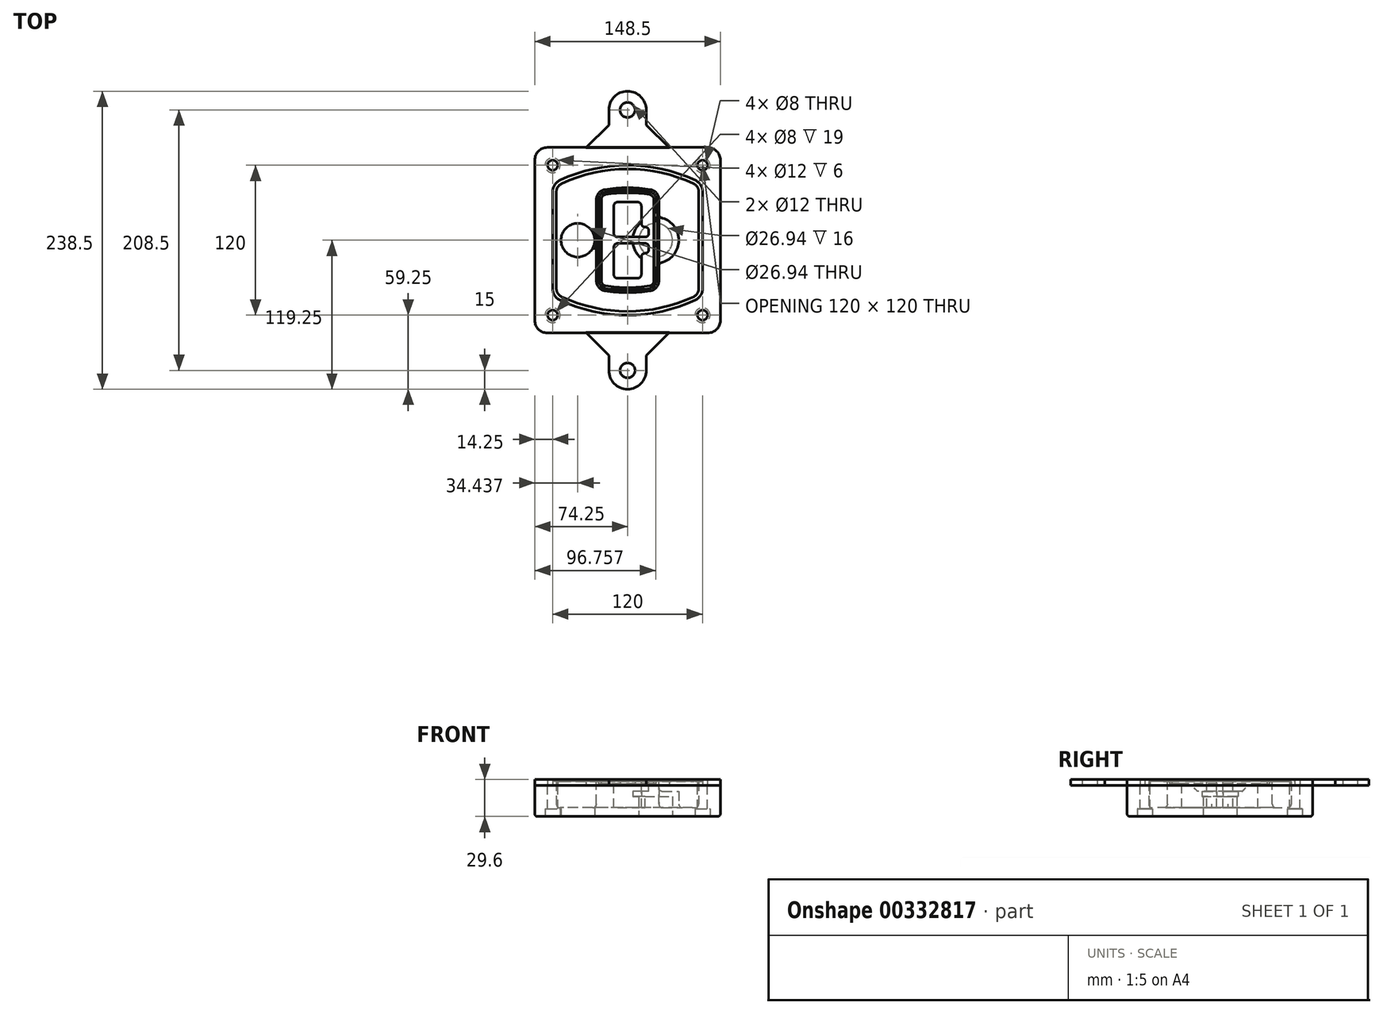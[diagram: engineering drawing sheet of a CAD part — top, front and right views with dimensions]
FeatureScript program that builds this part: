
annotation { "Feature Type Name" : "Feature", "Feature Type Description" : "" }
export const myFeature = defineFeature(function(context is Context, id is Id, definition is map)
    precondition{}
    {
        {
            var Q0;
            Q0=qCreatedBy(makeId("Top.planeOp"),FACE);
            var sketch = newSketch(context, id + "F0", { "sketchPlane" : qUnion([Q0])});
            skPoint(sketch, "E0.rect.middle", {"position": v(0, 0) * mm});
            skLineSegment(sketch, "E1.bottom", {"start": v(-64.25, -74.25) * mm, "end": v(64.25, -74.25) * mm});
            skLineSegment(sketch, "E1.top", {"start": v(-64.25, 74.25) * mm, "end": v(64.25, 74.25) * mm});
            skLineSegment(sketch, "E1.left", {"start": v(-74.25, -64.25) * mm, "end": v(-74.25, 64.25) * mm});
            skLineSegment(sketch, "E1.right", {"start": v(74.25, -64.25) * mm, "end": v(74.25, 64.25) * mm});
            skLineSegment(sketch, "E2", {"start": v(-74.25, 74.25) * mm, "end": v(74.25, -74.25) * mm, "construction": true});
            skLineSegment(sketch, "E3", {"start": v(74.25, 74.25) * mm, "end": v(-74.25, -74.25) * mm, "construction": true});
            skCircle(sketch, "E4", {"center": v(-60, 60) * mm, "radius": 4 * mm});
            skCircle(sketch, "E5", {"center": v(60, 60) * mm, "radius": 4 * mm});
            skCircle(sketch, "E6", {"center": v(60, -60) * mm, "radius": 4 * mm});
            skCircle(sketch, "E7", {"center": v(-60, -60) * mm, "radius": 4 * mm});
            skLineSegment(sketch, "E8", {"start": v(-60, 60) * mm, "end": v(60, 60) * mm, "construction": true});
            skLineSegment(sketch, "E9", {"start": v(60, 60) * mm, "end": v(60, -60) * mm, "construction": true});
            skLineSegment(sketch, "E10", {"start": v(60, -60) * mm, "end": v(-60, -60) * mm, "construction": true});
            skLineSegment(sketch, "E11", {"start": v(-60, -60) * mm, "end": v(-60, 60) * mm, "construction": true});
            skLineSegment(sketch, "E12", {"start": v(-60, 38.83) * mm, "end": v(-60, -38.83) * mm});
            skLineSegment(sketch, "E13", {"start": v(60, 38.83) * mm, "end": v(60, -38.83) * mm});
            skArc(sketch, "E14", {"start": v(54.26, 47.88) * mm, "mid": v(0, 60) * mm, "end": v(-54.26, 47.88) * mm});
            skArc(sketch, "E15", {"start": v(-54.26, -47.88) * mm, "mid": v(0, -60) * mm, "end": v(54.26, -47.88) * mm});
            skLineSegment(sketch, "E16", {"start": v(-60, 0) * mm, "end": v(60, 0) * mm, "construction": true});
            skPoint(sketch, "E17.visualSharp", {"position": v(-60, -45) * mm});
            skArc(sketch, "E17.filletArc", {"start": v(-60, -38.83) * mm, "mid": v(-58.44, -44.2) * mm, "end": v(-54.26, -47.88) * mm});
            skPoint(sketch, "E18.visualSharp", {"position": v(-60, 45) * mm});
            skArc(sketch, "E18.filletArc", {"start": v(-54.26, 47.88) * mm, "mid": v(-58.44, 44.2) * mm, "end": v(-60, 38.83) * mm});
            skPoint(sketch, "E19.visualSharp", {"position": v(60, 45) * mm});
            skArc(sketch, "E19.filletArc", {"start": v(60, 38.83) * mm, "mid": v(58.44, 44.2) * mm, "end": v(54.26, 47.88) * mm});
            skPoint(sketch, "E20.visualSharp", {"position": v(60, -45) * mm});
            skArc(sketch, "E20.filletArc", {"start": v(54.26, -47.88) * mm, "mid": v(58.44, -44.2) * mm, "end": v(60, -38.83) * mm});
            skPoint(sketch, "E21.visualSharp", {"position": v(-74.25, 74.25) * mm});
            skArc(sketch, "E21.filletArc", {"start": v(-64.25, 74.25) * mm, "mid": v(-71.32, 71.32) * mm, "end": v(-74.25, 64.25) * mm});
            skPoint(sketch, "E22.visualSharp", {"position": v(74.25, 74.25) * mm});
            skArc(sketch, "E22.filletArc", {"start": v(74.25, 64.25) * mm, "mid": v(71.32, 71.32) * mm, "end": v(64.25, 74.25) * mm});
            skPoint(sketch, "E23.visualSharp", {"position": v(74.25, -74.25) * mm});
            skArc(sketch, "E23.filletArc", {"start": v(64.25, -74.25) * mm, "mid": v(71.32, -71.32) * mm, "end": v(74.25, -64.25) * mm});
            skPoint(sketch, "E24.visualSharp", {"position": v(-74.25, -74.25) * mm});
            skArc(sketch, "E24.filletArc", {"start": v(-74.25, -64.25) * mm, "mid": v(-71.32, -71.32) * mm, "end": v(-64.25, -74.25) * mm});
            skArc(sketch, "E25.0", {"start": v(57, 38.83) * mm, "mid": v(55.9, 42.58) * mm, "end": v(52.98, 45.17) * mm});
            skLineSegment(sketch, "E25.1", {"start": v(57, 38.83) * mm, "end": v(57, -38.83) * mm});
            skArc(sketch, "E25.2", {"start": v(52.98, -45.17) * mm, "mid": v(55.9, -42.58) * mm, "end": v(57, -38.83) * mm});
            skArc(sketch, "E25.3", {"start": v(-52.98, -45.17) * mm, "mid": v(0, -57) * mm, "end": v(52.98, -45.17) * mm});
            skArc(sketch, "E25.4", {"start": v(-57, -38.83) * mm, "mid": v(-55.9, -42.58) * mm, "end": v(-52.98, -45.17) * mm});
            skArc(sketch, "E25.5", {"start": v(52.98, 45.17) * mm, "mid": v(0, 57) * mm, "end": v(-52.98, 45.17) * mm});
            skLineSegment(sketch, "E25.6", {"start": v(-57, 38.83) * mm, "end": v(-57, -38.83) * mm});
            skArc(sketch, "E25.7", {"start": v(-52.98, 45.17) * mm, "mid": v(-55.9, 42.58) * mm, "end": v(-57, 38.83) * mm});
            skArc(sketch, "E26.0", {"start": v(-55.96, 51.5) * mm, "mid": v(-61.82, 46.33) * mm, "end": v(-64, 38.83) * mm});
            skArc(sketch, "E26.1", {"start": v(55.96, 51.5) * mm, "mid": v(0, 64) * mm, "end": v(-55.96, 51.5) * mm});
            skArc(sketch, "E26.2", {"start": v(64, 38.83) * mm, "mid": v(61.82, 46.33) * mm, "end": v(55.96, 51.5) * mm});
            skLineSegment(sketch, "E26.3", {"start": v(64, 38.83) * mm, "end": v(64, -38.83) * mm});
            skArc(sketch, "E26.4", {"start": v(55.96, -51.5) * mm, "mid": v(61.82, -46.33) * mm, "end": v(64, -38.83) * mm});
            skLineSegment(sketch, "E26.5", {"start": v(-64, 38.83) * mm, "end": v(-64, -38.83) * mm});
            skArc(sketch, "E26.6", {"start": v(-55.96, -51.5) * mm, "mid": v(0, -64) * mm, "end": v(55.96, -51.5) * mm});
            skArc(sketch, "E26.7", {"start": v(-64, -38.83) * mm, "mid": v(-61.82, -46.33) * mm, "end": v(-55.96, -51.5) * mm});
            skSolve(sketch);
        }
        {
            var Q0;
            Q0=makeQuery(id+"F0.imprint","IMPRINT",FACE,{"disambiguationData":[TD([[makeQuery(id+"F0.imprint","IMPRINT",EDGE,{"derivedFrom":sQuery(id+"F0.wireOp",EDGE,"E1.bottom")}),1.0]])]});
            var Q1;
            Q1=makeQuery(id+"F0.imprint","IMPRINT",FACE,{"disambiguationData":[TD([[makeQuery(id+"F0.imprint","IMPRINT",EDGE,{"derivedFrom":sQuery(id+"F0.wireOp",EDGE,"E12")}),1.0]])]});
            var Q2;
            Q2=makeQuery(id+"F0.imprint","IMPRINT",FACE,{"disambiguationData":[TD([[makeQuery(id+"F0.imprint","IMPRINT",EDGE,{"derivedFrom":sQuery(id+"F0.wireOp",EDGE,"E25.0")}),1.0]])]});
            var Q3;
            Q3=makeQuery(id+"F0.imprint","IMPRINT",FACE,{"disambiguationData":[TD([[makeQuery(id+"F0.imprint","IMPRINT",EDGE,{"derivedFrom":sQuery(id+"F0.wireOp",EDGE,"E12")}),-1.0]])]});
            extrude(context, id + "F1", {"entities" : qUnion([Q0, Q1, Q2, Q3]), "oppositeDirection" : true, "depth" : 25 * mm});
        }
        {
            var Q0;
            Q0=makeQuery(id+"F0.imprint","IMPRINT",FACE,{"disambiguationData":[TD([[makeQuery(id+"F0.imprint","IMPRINT",EDGE,{"derivedFrom":sQuery(id+"F0.wireOp",EDGE,"E12")}),1.0]])]});
            extrude(context, id + "F2", {"entities" : qUnion([Q0]), "operationType" : NewBodyOperationType.ADD, "depth" : 3 * mm});
        }
        {
            var Q0;
            Q0=makeQuery(id+"F0.imprint","IMPRINT",FACE,{"disambiguationData":[TD([[makeQuery(id+"F0.imprint","IMPRINT",EDGE,{"derivedFrom":sQuery(id+"F0.wireOp",EDGE,"E25.0")}),1.0]])]});
            extrude(context, id + "F3", {"entities" : qUnion([Q0]), "operationType" : NewBodyOperationType.REMOVE, "oppositeDirection" : true, "depth" : 18 * mm});
        }
        {
            var Q0;
            Q0=makeQuery(id+"F2.opExtrude","CAP_FACE",FACE,{"disambiguationData":[OSD([sQuery(id+"F0.wireOp",EDGE,"E12"),sQuery(id+"F0.wireOp",EDGE,"E13"),sQuery(id+"F0.wireOp",EDGE,"E14"),sQuery(id+"F0.wireOp",EDGE,"E15"),sQuery(id+"F0.wireOp",EDGE,"E17.filletArc"),sQuery(id+"F0.wireOp",EDGE,"E18.filletArc"),sQuery(id+"F0.wireOp",EDGE,"E19.filletArc"),sQuery(id+"F0.wireOp",EDGE,"E20.filletArc"),sQuery(id+"F0.wireOp",EDGE,"E25.0"),sQuery(id+"F0.wireOp",EDGE,"E25.1"),sQuery(id+"F0.wireOp",EDGE,"E25.2"),sQuery(id+"F0.wireOp",EDGE,"E25.3"),sQuery(id+"F0.wireOp",EDGE,"E25.4"),sQuery(id+"F0.wireOp",EDGE,"E25.5"),sQuery(id+"F0.wireOp",EDGE,"E25.6"),sQuery(id+"F0.wireOp",EDGE,"E25.7")])],"isStart":false});
            var sketch = newSketch(context, id + "F4", { "sketchPlane" : qUnion([Q0])});
            skArc(sketch, "E27.0", {"start": v(-18.34, -40.45) * mm, "mid": v(0, -42) * mm, "end": v(18.34, -40.45) * mm});
            skArc(sketch, "E28.0", {"start": v(18.34, 40.45) * mm, "mid": v(0, 42) * mm, "end": v(-18.34, 40.45) * mm});
            skLineSegment(sketch, "E29", {"start": v(-25, 32.57) * mm, "end": v(-25, -32.57) * mm});
            skLineSegment(sketch, "E30", {"start": v(25, 32.57) * mm, "end": v(25, -32.57) * mm});
            skLineSegment(sketch, "E31", {"start": v(-25, 39.1) * mm, "end": v(25, 39.1) * mm, "construction": true});
            skLineSegment(sketch, "E32", {"start": v(-25, -39.1) * mm, "end": v(25, -39.1) * mm, "construction": true});
            skPoint(sketch, "E33.visualSharp", {"position": v(-25, 39.1) * mm});
            skArc(sketch, "E33.filletArc", {"start": v(-18.34, 40.45) * mm, "mid": v(-23.11, 37.73) * mm, "end": v(-25, 32.57) * mm});
            skPoint(sketch, "E34.visualSharp", {"position": v(25, 39.1) * mm});
            skArc(sketch, "E34.filletArc", {"start": v(25, 32.57) * mm, "mid": v(23.11, 37.73) * mm, "end": v(18.34, 40.45) * mm});
            skPoint(sketch, "E35.visualSharp", {"position": v(25, -39.1) * mm});
            skArc(sketch, "E35.filletArc", {"start": v(18.34, -40.45) * mm, "mid": v(23.11, -37.73) * mm, "end": v(25, -32.57) * mm});
            skPoint(sketch, "E36.visualSharp", {"position": v(-25, -39.1) * mm});
            skArc(sketch, "E36.filletArc", {"start": v(-25, -32.57) * mm, "mid": v(-23.11, -37.73) * mm, "end": v(-18.34, -40.45) * mm});
            skArc(sketch, "E37.0", {"start": v(52.98, 45.17) * mm, "mid": v(0, 57) * mm, "end": v(-52.98, 45.17) * mm});
            skArc(sketch, "E37.1", {"start": v(-52.98, 45.17) * mm, "mid": v(-55.9, 42.58) * mm, "end": v(-57, 38.83) * mm});
            skLineSegment(sketch, "E37.2", {"start": v(-57, 38.83) * mm, "end": v(-57, -38.83) * mm});
            skArc(sketch, "E37.3", {"start": v(-57, -38.83) * mm, "mid": v(-55.9, -42.58) * mm, "end": v(-52.98, -45.17) * mm});
            skArc(sketch, "E37.4", {"start": v(-52.98, -45.17) * mm, "mid": v(0, -57) * mm, "end": v(52.98, -45.17) * mm});
            skArc(sketch, "E37.5", {"start": v(52.98, -45.17) * mm, "mid": v(55.9, -42.58) * mm, "end": v(57, -38.83) * mm});
            skLineSegment(sketch, "E37.6", {"start": v(57, 38.83) * mm, "end": v(57, -38.83) * mm});
            skArc(sketch, "E37.7", {"start": v(57, 38.83) * mm, "mid": v(55.9, 42.58) * mm, "end": v(52.98, 45.17) * mm});
            skLineSegment(sketch, "E38.0", {"start": v(23, 32.57) * mm, "end": v(23, -32.57) * mm});
            skArc(sketch, "E38.1", {"start": v(18, -38.48) * mm, "mid": v(21.58, -36.44) * mm, "end": v(23, -32.57) * mm});
            skArc(sketch, "E38.2", {"start": v(-18, -38.48) * mm, "mid": v(0, -40) * mm, "end": v(18, -38.48) * mm});
            skArc(sketch, "E38.3", {"start": v(-23, -32.57) * mm, "mid": v(-21.58, -36.44) * mm, "end": v(-18, -38.48) * mm});
            skLineSegment(sketch, "E38.4", {"start": v(-23, 32.57) * mm, "end": v(-23, -32.57) * mm});
            skArc(sketch, "E38.5", {"start": v(23, 32.57) * mm, "mid": v(21.58, 36.44) * mm, "end": v(18, 38.48) * mm});
            skArc(sketch, "E38.6", {"start": v(-18, 38.48) * mm, "mid": v(-21.58, 36.44) * mm, "end": v(-23, 32.57) * mm});
            skArc(sketch, "E38.7", {"start": v(18, 38.48) * mm, "mid": v(0, 40) * mm, "end": v(-18, 38.48) * mm});
            skArc(sketch, "E39.0", {"start": v(21, 32.57) * mm, "mid": v(20.06, 35.15) * mm, "end": v(17.67, 36.5) * mm});
            skLineSegment(sketch, "E39.1", {"start": v(21, 32.57) * mm, "end": v(21, -32.57) * mm});
            skArc(sketch, "E39.2", {"start": v(17.67, -36.5) * mm, "mid": v(20.06, -35.15) * mm, "end": v(21, -32.57) * mm});
            skArc(sketch, "E39.3", {"start": v(-17.67, -36.5) * mm, "mid": v(0, -38) * mm, "end": v(17.67, -36.5) * mm});
            skArc(sketch, "E39.4", {"start": v(-21, -32.57) * mm, "mid": v(-20.06, -35.15) * mm, "end": v(-17.67, -36.5) * mm});
            skArc(sketch, "E39.5", {"start": v(17.67, 36.5) * mm, "mid": v(0, 38) * mm, "end": v(-17.67, 36.5) * mm});
            skLineSegment(sketch, "E39.6", {"start": v(-21, 32.57) * mm, "end": v(-21, -32.57) * mm});
            skArc(sketch, "E39.7", {"start": v(-17.67, 36.5) * mm, "mid": v(-20.06, 35.15) * mm, "end": v(-21, 32.57) * mm});
            skLineSegment(sketch, "E40", {"start": v(-25, 0) * mm, "end": v(25, 0) * mm, "construction": true});
            skLineSegment(sketch, "E41", {"start": v(-11, 5.5) * mm, "end": v(-11, 27.5) * mm});
            skLineSegment(sketch, "E42", {"start": v(-8, 30.5) * mm, "end": v(8, 30.5) * mm});
            skLineSegment(sketch, "E43", {"start": v(11, 27.5) * mm, "end": v(11, 13.5) * mm});
            skLineSegment(sketch, "E44", {"start": v(14, 10.5) * mm, "end": v(14, 10.5) * mm});
            skLineSegment(sketch, "E45", {"start": v(17, 7.5) * mm, "end": v(17, 5.5) * mm});
            skLineSegment(sketch, "E46", {"start": v(14, 2.5) * mm, "end": v(-8, 2.5) * mm});
            skPoint(sketch, "E47.visualSharp", {"position": v(-11, 30.5) * mm});
            skArc(sketch, "E47.filletArc", {"start": v(-8, 30.5) * mm, "mid": v(-10.12, 29.62) * mm, "end": v(-11, 27.5) * mm});
            skPoint(sketch, "E48.visualSharp", {"position": v(11, 30.5) * mm});
            skArc(sketch, "E48.filletArc", {"start": v(11, 27.5) * mm, "mid": v(10.12, 29.62) * mm, "end": v(8, 30.5) * mm});
            skPoint(sketch, "E49.visualSharp", {"position": v(11, 10.5) * mm});
            skArc(sketch, "E49.filletArc", {"start": v(11, 13.5) * mm, "mid": v(11.88, 11.38) * mm, "end": v(14, 10.5) * mm});
            skPoint(sketch, "E50.visualSharp", {"position": v(17, 10.5) * mm});
            skArc(sketch, "E50.filletArc", {"start": v(17, 7.5) * mm, "mid": v(16.12, 9.62) * mm, "end": v(14, 10.5) * mm});
            skPoint(sketch, "E51.visualSharp", {"position": v(17, 2.5) * mm});
            skArc(sketch, "E51.filletArc", {"start": v(14, 2.5) * mm, "mid": v(16.12, 3.38) * mm, "end": v(17, 5.5) * mm});
            skPoint(sketch, "E52.visualSharp", {"position": v(-11, 2.5) * mm});
            skArc(sketch, "E52.filletArc", {"start": v(-11, 5.5) * mm, "mid": v(-10.12, 3.38) * mm, "end": v(-8, 2.5) * mm});
            skLineSegment(sketch, "E53.0.MirrorCS", {"start": v(14, -2.5) * mm, "end": v(-8, -2.5) * mm});
            skArc(sketch, "E54.0.MirrorCS", {"start": v(-11, -5.5) * mm, "mid": v(-10.12, -3.38) * mm, "end": v(-8, -2.5) * mm});
            skLineSegment(sketch, "E55.0.MirrorCS", {"start": v(-11, -5.5) * mm, "end": v(-11, -27.5) * mm});
            skArc(sketch, "E56.0.MirrorCS", {"start": v(-8, -30.5) * mm, "mid": v(-10.12, -29.62) * mm, "end": v(-11, -27.5) * mm});
            skLineSegment(sketch, "E57.0.MirrorCS", {"start": v(-8, -30.5) * mm, "end": v(8, -30.5) * mm});
            skArc(sketch, "E58.0.MirrorCS", {"start": v(11, -27.5) * mm, "mid": v(10.12, -29.62) * mm, "end": v(8, -30.5) * mm});
            skLineSegment(sketch, "E59.0.MirrorCS", {"start": v(11, -27.5) * mm, "end": v(11, -13.5) * mm});
            skArc(sketch, "E60.0.MirrorCS", {"start": v(11, -13.5) * mm, "mid": v(11.88, -11.38) * mm, "end": v(14, -10.5) * mm});
            skArc(sketch, "E61.0.MirrorCS", {"start": v(17, -7.5) * mm, "mid": v(16.12, -9.62) * mm, "end": v(14, -10.5) * mm});
            skLineSegment(sketch, "E62.0.MirrorCS", {"start": v(17, -7.5) * mm, "end": v(17, -5.5) * mm});
            skArc(sketch, "E63.0.MirrorCS", {"start": v(14, -2.5) * mm, "mid": v(16.12, -3.38) * mm, "end": v(17, -5.5) * mm});
            skSolve(sketch);
        }
        {
            var Q0;
            Q0=makeQuery(id+"F4.imprint","IMPRINT",FACE,{"disambiguationData":[TD([[makeQuery(id+"F4.imprint","IMPRINT",EDGE,{"derivedFrom":sQuery(id+"F4.wireOp",EDGE,"E27.0")}),1.0]])]});
            var Q1;
            Q1=makeQuery(id+"F4.imprint","IMPRINT",FACE,{"disambiguationData":[TD([[makeQuery(id+"F4.imprint","IMPRINT",EDGE,{"derivedFrom":sQuery(id+"F4.wireOp",EDGE,"E38.0")}),-1.0]])]});
            var Q2;
            Q2=makeQuery(id+"F4.imprint","IMPRINT",FACE,{"disambiguationData":[TD([[makeQuery(id+"F4.imprint","IMPRINT",EDGE,{"derivedFrom":sQuery(id+"F4.wireOp",EDGE,"E39.0")}),1.0]])]});
            extrude(context, id + "F5", {"entities" : qUnion([Q0, Q1, Q2]), "operationType" : NewBodyOperationType.ADD, "endBound" : BoundingType.UP_TO_NEXT, "oppositeDirection" : true, "depth" : 25 * mm});
        }
        {
            var Q0;
            Q0=makeQuery(id+"F4.imprint","IMPRINT",FACE,{"disambiguationData":[TD([[makeQuery(id+"F4.imprint","IMPRINT",EDGE,{"derivedFrom":sQuery(id+"F4.wireOp",EDGE,"E38.0")}),-1.0]])]});
            extrude(context, id + "F6", {"entities" : qUnion([Q0]), "operationType" : NewBodyOperationType.REMOVE, "oppositeDirection" : true, "depth" : 2 * mm});
        }
        {
            var Q0;
            Q0=makeQuery(id+"F1.opExtrude","CAP_FACE",FACE,{"disambiguationData":[OSD([sQuery(id+"F0.wireOp",EDGE,"E1.bottom"),sQuery(id+"F0.wireOp",EDGE,"E1.top"),sQuery(id+"F0.wireOp",EDGE,"E1.left"),sQuery(id+"F0.wireOp",EDGE,"E1.right"),sQuery(id+"F0.wireOp",EDGE,"E4"),sQuery(id+"F0.wireOp",EDGE,"E5"),sQuery(id+"F0.wireOp",EDGE,"E6"),sQuery(id+"F0.wireOp",EDGE,"E7"),sQuery(id+"F0.wireOp",EDGE,"E21.filletArc"),sQuery(id+"F0.wireOp",EDGE,"E22.filletArc"),sQuery(id+"F0.wireOp",EDGE,"E23.filletArc"),sQuery(id+"F0.wireOp",EDGE,"E24.filletArc")])],"isStart":false});
            var sketch = newSketch(context, id + "F7", { "sketchPlane" : qUnion([Q0])});
            skCircle(sketch, "E64", {"center": v(22.5, 0) * mm, "radius": 13.47 * mm});
            skCircle(sketch, "E65", {"center": v(-39.81, 0) * mm, "radius": 13.47 * mm});
            skLineSegment(sketch, "E66", {"start": v(74.25, 0) * mm, "end": v(-74.25, 0) * mm});
            skCircle(sketch, "E67", {"center": v(22.5, 0) * mm, "radius": 18.47 * mm});
            skCircle(sketch, "E68", {"center": v(60, -60) * mm, "radius": 6 * mm});
            skCircle(sketch, "E69", {"center": v(-60, -60) * mm, "radius": 6 * mm});
            skCircle(sketch, "E70", {"center": v(-60, 60) * mm, "radius": 6 * mm});
            skCircle(sketch, "E71", {"center": v(60, 60) * mm, "radius": 6 * mm});
            skSolve(sketch);
        }
        {
            var Q0;
            {var subQ1=sQuery(id+"F7.wireOp",EDGE,"E66");var subQ4=sQuery(id+"F7.wireOp",EDGE,"E64");var subQ6=makeQuery(id+"F7.imprint","INTERSECT",VERTEX,{"disambiguationData":[OD(0.0)],"derivedFrom":[subQ4,subQ1]});Q0=makeQuery(id+"F7.imprint","IMPRINT",FACE,{"disambiguationData":[TD([[makeQuery(id+"F7.imprint","IMPRINT",EDGE,{"disambiguationData":[TD([[subQ6,-1.0]])],"derivedFrom":subQ4}),-1.0]])]});}
            var Q1;
            {var subQ0=sQuery(id+"F7.wireOp",EDGE,"E66");var subQ1=sQuery(id+"F7.wireOp",EDGE,"E64");var subQ3=makeQuery(id+"F7.imprint","INTERSECT",VERTEX,{"disambiguationData":[OD(0.0)],"derivedFrom":[subQ1,subQ0]});Q1=makeQuery(id+"F7.imprint","IMPRINT",FACE,{"disambiguationData":[TD([[makeQuery(id+"F7.imprint","IMPRINT",EDGE,{"disambiguationData":[TD([[subQ3,-1.0]])],"derivedFrom":subQ1}),1.0]])]});}
            var Q2;
            {var subQ0=sQuery(id+"F7.wireOp",EDGE,"E66");var subQ1=sQuery(id+"F7.wireOp",EDGE,"E64");var subQ3=makeQuery(id+"F7.imprint","INTERSECT",VERTEX,{"disambiguationData":[OD(0.0)],"derivedFrom":[subQ1,subQ0]});Q2=makeQuery(id+"F7.imprint","IMPRINT",FACE,{"disambiguationData":[TD([[makeQuery(id+"F7.imprint","IMPRINT",EDGE,{"disambiguationData":[TD([[subQ3,1.0]])],"derivedFrom":subQ1}),1.0]])]});}
            var Q3;
            {var subQ1=sQuery(id+"F7.wireOp",EDGE,"E66");var subQ4=sQuery(id+"F7.wireOp",EDGE,"E64");var subQ6=makeQuery(id+"F7.imprint","INTERSECT",VERTEX,{"disambiguationData":[OD(0.0)],"derivedFrom":[subQ4,subQ1]});Q3=makeQuery(id+"F7.imprint","IMPRINT",FACE,{"disambiguationData":[TD([[makeQuery(id+"F7.imprint","IMPRINT",EDGE,{"disambiguationData":[TD([[subQ6,1.0]])],"derivedFrom":subQ4}),-1.0]])]});}
            extrude(context, id + "F8", {"entities" : qUnion([Q0, Q1, Q2, Q3]), "operationType" : NewBodyOperationType.ADD, "oppositeDirection" : true, "depth" : 20 * mm});
        }
        {
            var Q0;
            {var subQ0=sQuery(id+"F7.wireOp",EDGE,"E66");var subQ1=sQuery(id+"F7.wireOp",EDGE,"E64");var subQ3=makeQuery(id+"F7.imprint","INTERSECT",VERTEX,{"disambiguationData":[OD(0.0)],"derivedFrom":[subQ1,subQ0]});Q0=makeQuery(id+"F7.imprint","IMPRINT",FACE,{"disambiguationData":[TD([[makeQuery(id+"F7.imprint","IMPRINT",EDGE,{"disambiguationData":[TD([[subQ3,-1.0]])],"derivedFrom":subQ1}),1.0]])]});}
            var Q1;
            {var subQ0=sQuery(id+"F7.wireOp",EDGE,"E66");var subQ1=sQuery(id+"F7.wireOp",EDGE,"E64");var subQ3=makeQuery(id+"F7.imprint","INTERSECT",VERTEX,{"disambiguationData":[OD(0.0)],"derivedFrom":[subQ1,subQ0]});Q1=makeQuery(id+"F7.imprint","IMPRINT",FACE,{"disambiguationData":[TD([[makeQuery(id+"F7.imprint","IMPRINT",EDGE,{"disambiguationData":[TD([[subQ3,1.0]])],"derivedFrom":subQ1}),1.0]])]});}
            extrude(context, id + "F9", {"entities" : qUnion([Q0, Q1]), "operationType" : NewBodyOperationType.REMOVE, "oppositeDirection" : true, "depth" : 16 * mm});
        }
        {
            var Q0;
            {var subQ0=sQuery(id+"F7.wireOp",EDGE,"E66");var subQ1=sQuery(id+"F7.wireOp",EDGE,"E65");var subQ3=makeQuery(id+"F7.imprint","INTERSECT",VERTEX,{"disambiguationData":[OD(0.0)],"derivedFrom":[subQ1,subQ0]});Q0=makeQuery(id+"F7.imprint","IMPRINT",FACE,{"disambiguationData":[TD([[makeQuery(id+"F7.imprint","IMPRINT",EDGE,{"disambiguationData":[TD([[subQ3,-1.0]])],"derivedFrom":subQ1}),1.0]])]});}
            var Q1;
            {var subQ0=sQuery(id+"F7.wireOp",EDGE,"E66");var subQ1=sQuery(id+"F7.wireOp",EDGE,"E65");var subQ3=makeQuery(id+"F7.imprint","INTERSECT",VERTEX,{"disambiguationData":[OD(0.0)],"derivedFrom":[subQ1,subQ0]});Q1=makeQuery(id+"F7.imprint","IMPRINT",FACE,{"disambiguationData":[TD([[makeQuery(id+"F7.imprint","IMPRINT",EDGE,{"disambiguationData":[TD([[subQ3,1.0]])],"derivedFrom":subQ1}),1.0]])]});}
            extrude(context, id + "F10", {"entities" : qUnion([Q0, Q1]), "operationType" : NewBodyOperationType.REMOVE, "oppositeDirection" : true, "depth" : 25 * mm});
        }
        {
            var Q0;
            Q0=makeQuery(id+"F7.imprint","IMPRINT",FACE,{"disambiguationData":[TD([[makeQuery(id+"F7.imprint","IMPRINT",EDGE,{"derivedFrom":sQuery(id+"F7.wireOp",EDGE,"E68")}),1.0]])]});
            var Q1;
            Q1=makeQuery(id+"F7.imprint","IMPRINT",FACE,{"disambiguationData":[TD([[makeQuery(id+"F7.imprint","IMPRINT",EDGE,{"derivedFrom":makeQuery(id+"F1.opExtrude","CAP_EDGE",EDGE,{"disambiguationData":[OSD([sQuery(id+"F0.wireOp",EDGE,"E5")])],"isStart":false})}),-1.0]])]});
            var Q2;
            Q2=makeQuery(id+"F7.imprint","IMPRINT",FACE,{"disambiguationData":[TD([[makeQuery(id+"F7.imprint","IMPRINT",EDGE,{"derivedFrom":sQuery(id+"F7.wireOp",EDGE,"E69")}),1.0]])]});
            var Q3;
            Q3=makeQuery(id+"F7.imprint","IMPRINT",FACE,{"disambiguationData":[TD([[makeQuery(id+"F7.imprint","IMPRINT",EDGE,{"derivedFrom":makeQuery(id+"F1.opExtrude","CAP_EDGE",EDGE,{"disambiguationData":[OSD([sQuery(id+"F0.wireOp",EDGE,"E4")])],"isStart":false})}),-1.0]])]});
            var Q4;
            Q4=makeQuery(id+"F7.imprint","IMPRINT",FACE,{"disambiguationData":[TD([[makeQuery(id+"F7.imprint","IMPRINT",EDGE,{"derivedFrom":sQuery(id+"F7.wireOp",EDGE,"E70")}),1.0]])]});
            var Q5;
            Q5=makeQuery(id+"F7.imprint","IMPRINT",FACE,{"disambiguationData":[TD([[makeQuery(id+"F7.imprint","IMPRINT",EDGE,{"derivedFrom":makeQuery(id+"F1.opExtrude","CAP_EDGE",EDGE,{"disambiguationData":[OSD([sQuery(id+"F0.wireOp",EDGE,"E7")])],"isStart":false})}),-1.0]])]});
            var Q6;
            Q6=makeQuery(id+"F7.imprint","IMPRINT",FACE,{"disambiguationData":[TD([[makeQuery(id+"F7.imprint","IMPRINT",EDGE,{"derivedFrom":sQuery(id+"F7.wireOp",EDGE,"E71")}),1.0]])]});
            var Q7;
            Q7=makeQuery(id+"F7.imprint","IMPRINT",FACE,{"disambiguationData":[TD([[makeQuery(id+"F7.imprint","IMPRINT",EDGE,{"derivedFrom":makeQuery(id+"F1.opExtrude","CAP_EDGE",EDGE,{"disambiguationData":[OSD([sQuery(id+"F0.wireOp",EDGE,"E6")])],"isStart":false})}),-1.0]])]});
            extrude(context, id + "F11", {"entities" : qUnion([Q0, Q1, Q2, Q3, Q4, Q5, Q6, Q7]), "operationType" : NewBodyOperationType.REMOVE, "oppositeDirection" : true, "depth" : 6 * mm});
        }
        {
            var Q0;
            Q0=makeQuery(id+"F9.boolean.opBoolean","COPY",FACE,{"derivedFrom":makeQuery(id+"F9.opExtrude","CAP_FACE",FACE,{"disambiguationData":[OSD([sQuery(id+"F7.wireOp",EDGE,"E64")])],"isStart":false})});
            var sketch = newSketch(context, id + "F12", { "sketchPlane" : qUnion([Q0])});
            skArc(sketch, "E72.0", {"start": v(11, 14.45) * mm, "mid": v(6.45, 9.13) * mm, "end": v(4.2, 2.5) * mm});
            skArc(sketch, "E72.1", {"start": v(4.2, -2.5) * mm, "mid": v(6.45, -9.13) * mm, "end": v(11, -14.45) * mm});
            skLineSegment(sketch, "E73", {"start": v(4.2, -2.5) * mm, "end": v(14, -2.5) * mm});
            skLineSegment(sketch, "E74.0", {"start": v(14, 2.5) * mm, "end": v(4.2, 2.5) * mm});
            skArc(sketch, "E74.1", {"start": v(14, 2.5) * mm, "mid": v(16.12, 3.38) * mm, "end": v(17, 5.5) * mm});
            skLineSegment(sketch, "E74.2", {"start": v(17, 7.5) * mm, "end": v(17, 5.5) * mm});
            skArc(sketch, "E74.3", {"start": v(17, 7.5) * mm, "mid": v(16.12, 9.62) * mm, "end": v(14, 10.5) * mm});
            skArc(sketch, "E74.4", {"start": v(11, 13.5) * mm, "mid": v(11.88, 11.38) * mm, "end": v(14, 10.5) * mm});
            skLineSegment(sketch, "E74.5", {"start": v(11, 14.45) * mm, "end": v(11, 13.5) * mm});
            skLineSegment(sketch, "E74.7", {"start": v(14, -2.5) * mm, "end": v(4.2, -2.5) * mm});
            skArc(sketch, "E74.8", {"start": v(14, -2.5) * mm, "mid": v(16.12, -3.38) * mm, "end": v(17, -5.5) * mm});
            skLineSegment(sketch, "E74.9", {"start": v(17, -7.5) * mm, "end": v(17, -5.5) * mm});
            skArc(sketch, "E74.10", {"start": v(17, -7.5) * mm, "mid": v(16.12, -9.62) * mm, "end": v(14, -10.5) * mm});
            skArc(sketch, "E74.11", {"start": v(11, -13.5) * mm, "mid": v(11.88, -11.38) * mm, "end": v(14, -10.5) * mm});
            skLineSegment(sketch, "E74.12", {"start": v(11, -14.45) * mm, "end": v(11, -13.5) * mm});
            skPoint(sketch, "E75.orphan", {"position": v(11, -27.5) * mm});
            skPoint(sketch, "E76.orphan", {"position": v(-8, -2.5) * mm});
            skPoint(sketch, "E77.orphan", {"position": v(-8, 2.5) * mm});
            skPoint(sketch, "E78.orphan", {"position": v(11, 27.5) * mm});
            skSolve(sketch);
        }
        {
            var Q0;
            {var subQ7=sQuery(id+"F12.wireOp",EDGE,"E72.0");var subQ14=sQuery(id+"F12.wireOp",EDGE,"E72.1");var subQ16=sQuery(id+"F12.wireOp",EDGE,"E74.1");var subQ18=sQuery(id+"F12.wireOp",EDGE,"E74.8");Q0=qUnion([makeQuery(id+"F12.imprint","IMPRINT",FACE,{"disambiguationData":[TD([[makeQuery(id+"F12.imprint","IMPRINT",EDGE,{"derivedFrom":subQ7}),1.0]])]}),makeQuery(id+"F12.imprint","IMPRINT",FACE,{"disambiguationData":[TD([[makeQuery(id+"F12.imprint","IMPRINT",EDGE,{"derivedFrom":subQ14}),1.0]])]}),makeQuery(id+"F12.imprint","IMPRINT",FACE,{"disambiguationData":[TD([[makeQuery(id+"F12.imprint","IMPRINT",EDGE,{"derivedFrom":subQ16}),1.0]])]}),makeQuery(id+"F12.imprint","IMPRINT",FACE,{"disambiguationData":[TD([[makeQuery(id+"F12.imprint","IMPRINT",EDGE,{"derivedFrom":subQ18}),-1.0]])]})]);}
            var Q1;
            Q1=makeQuery(id+"F5.boolean.opBoolean","SPLIT",FACE,{"disambiguationData":[TD([makeQuery(id+"F5.opExtrude","SWEPT_FACE",FACE,{"disambiguationData":[OSD([sQuery(id+"F4.wireOp",EDGE,"E41")])]})])],"derivedFrom":makeQuery(id+"F3.boolean.opBoolean","COPY",FACE,{"derivedFrom":makeQuery(id+"F3.opExtrude","CAP_FACE",FACE,{"disambiguationData":[OSD([sQuery(id+"F0.wireOp",EDGE,"E25.0"),sQuery(id+"F0.wireOp",EDGE,"E25.1"),sQuery(id+"F0.wireOp",EDGE,"E25.2"),sQuery(id+"F0.wireOp",EDGE,"E25.3"),sQuery(id+"F0.wireOp",EDGE,"E25.4"),sQuery(id+"F0.wireOp",EDGE,"E25.5"),sQuery(id+"F0.wireOp",EDGE,"E25.6"),sQuery(id+"F0.wireOp",EDGE,"E25.7")])],"isStart":false})})});
            extrude(context, id + "F13", {"entities" : qUnion([Q0]), "operationType" : NewBodyOperationType.REMOVE, "endBound" : BoundingType.UP_TO_SURFACE, "endBoundEntityFace" : qUnion([Q1]), "depth" : 25 * mm});
        }
        {
            var Q0;
            Q0=makeQuery(id+"F3.boolean.opBoolean","COPY",EDGE,{"derivedFrom":makeQuery(id+"F3.opExtrude","CAP_EDGE",EDGE,{"disambiguationData":[OSD([sQuery(id+"F0.wireOp",EDGE,"E25.6")])],"isStart":false})});
            var Q1;
            Q1=makeQuery(id+"F8.boolean.opBoolean","INTERSECT",EDGE,{"derivedFrom":[makeQuery(id+"F5.opExtrude","SWEPT_FACE",FACE,{"disambiguationData":[OSD([sQuery(id+"F4.wireOp",EDGE,"E30")])]}),makeQuery(id+"F8.opExtrude","CAP_FACE",FACE,{"disambiguationData":[OSD([sQuery(id+"F7.wireOp",EDGE,"E67")])],"isStart":false})]});
            var Q2;
            Q2=makeQuery(id+"F8.boolean.opBoolean","INTERSECT",EDGE,{"disambiguationData":[OD(1.0)],"derivedFrom":[makeQuery(id+"F5.opExtrude","SWEPT_FACE",FACE,{"disambiguationData":[OSD([sQuery(id+"F4.wireOp",EDGE,"E30")])]}),makeQuery(id+"F8.opExtrude","SWEPT_FACE",FACE,{"disambiguationData":[OSD([sQuery(id+"F7.wireOp",EDGE,"E67")])]})]});
            var Q3;
            {var subQ0=sQuery(id+"F4.wireOp",EDGE,"E30");Q3=makeQuery(id+"F8.boolean.opBoolean","SPLIT",EDGE,{"disambiguationData":[TD([makeQuery(id+"F5.opExtrude","SWEPT_FACE",FACE,{"disambiguationData":[OSD([sQuery(id+"F4.wireOp",EDGE,"E35.filletArc")])]})])],"derivedFrom":makeQuery(id+"F5.opExtrude","CAP_EDGE",EDGE,{"disambiguationData":[OSD([subQ0])],"isStart":false})});}
            var Q4;
            {var subQ0=sQuery(id+"F0.wireOp",EDGE,"E25.7");var subQ1=sQuery(id+"F0.wireOp",EDGE,"E25.1");var subQ2=sQuery(id+"F0.wireOp",EDGE,"E25.6");var subQ3=sQuery(id+"F0.wireOp",EDGE,"E25.5");var subQ4=sQuery(id+"F0.wireOp",EDGE,"E25.4");var subQ5=sQuery(id+"F0.wireOp",EDGE,"E25.0");var subQ6=sQuery(id+"F0.wireOp",EDGE,"E25.2");var subQ7=sQuery(id+"F0.wireOp",EDGE,"E25.3");Q4=makeQuery(id+"F8.boolean.opBoolean","INTERSECT",EDGE,{"derivedFrom":[makeQuery(id+"F5.boolean.opBoolean","SPLIT",FACE,{"disambiguationData":[TD([makeQuery(id+"F2.opExtrude","SWEPT_FACE",FACE,{"disambiguationData":[OSD([subQ5])]})])],"derivedFrom":makeQuery(id+"F3.boolean.opBoolean","COPY",FACE,{"derivedFrom":makeQuery(id+"F3.opExtrude","CAP_FACE",FACE,{"disambiguationData":[OSD([subQ5,subQ1,subQ6,subQ7,subQ4,subQ3,subQ2,subQ0])],"isStart":false})})}),makeQuery(id+"F8.opExtrude","SWEPT_FACE",FACE,{"disambiguationData":[OSD([sQuery(id+"F7.wireOp",EDGE,"E67")])]})]});}
            var Q5;
            Q5=makeQuery(id+"F8.boolean.opBoolean","INTERSECT",EDGE,{"disambiguationData":[OD(0.0)],"derivedFrom":[makeQuery(id+"F5.opExtrude","SWEPT_FACE",FACE,{"disambiguationData":[OSD([sQuery(id+"F4.wireOp",EDGE,"E30")])]}),makeQuery(id+"F8.opExtrude","SWEPT_FACE",FACE,{"disambiguationData":[OSD([sQuery(id+"F7.wireOp",EDGE,"E67")])]})]});
            fillet(context, id + "F14", {"entities" : qUnion([Q0, Q1, Q2, Q3, Q4, Q5]), "radius" : 3 * mm, "tangentPropagation" : true, "allowEdgeOverflow" : false});
        }
        {
            var Q0;
            Q0=makeQuery(id+"F1.opExtrude","CAP_EDGE",EDGE,{"disambiguationData":[OSD([sQuery(id+"F0.wireOp",EDGE,"E1.bottom")])],"isStart":false});
            fillet(context, id + "F15", {"entities" : qUnion([Q0]), "radius" : 2 * mm, "tangentPropagation" : true, "allowEdgeOverflow" : false});
        }
        {
            var Q0;
            Q0=qCreatedBy(makeId("Top.planeOp"),FACE);
            var sketch = newSketch(context, id + "F16", { "sketchPlane" : qUnion([Q0])});
            skLineSegment(sketch, "E79", {"start": v(0, 73.96) * mm, "end": v(0, 104.25) * mm, "construction": true});
            skCircle(sketch, "E80", {"center": v(0, 104.25) * mm, "radius": 6 * mm});
            skLineSegment(sketch, "E81", {"start": v(15, 92.25) * mm, "end": v(33.29, 73.96) * mm});
            skLineSegment(sketch, "E82", {"start": v(-15, 92.25) * mm, "end": v(-15, 104.25) * mm});
            skLineSegment(sketch, "E83", {"start": v(15, 92.25) * mm, "end": v(15, 104.25) * mm});
            skArc(sketch, "E84", {"start": v(15, 104.25) * mm, "mid": v(0, 119.25) * mm, "end": v(-15, 104.25) * mm});
            skLineSegment(sketch, "E85", {"start": v(-15, 92.25) * mm, "end": v(-33.29, 73.96) * mm});
            skLineSegment(sketch, "E86", {"start": v(-74.17, 0) * mm, "end": v(74.38, 0) * mm, "construction": true});
            skArc(sketch, "E87.MirrorCS", {"start": v(15, -104.25) * mm, "mid": v(0, -119.25) * mm, "end": v(-15, -104.25) * mm});
            skCircle(sketch, "E88.MirrorC", {"center": v(0, -104.25) * mm, "radius": 6 * mm});
            skLineSegment(sketch, "E89.MirrorCS", {"start": v(0, -73.96) * mm, "end": v(0, -104.25) * mm, "construction": true});
            skLineSegment(sketch, "E90.MirrorCS", {"start": v(15, -92.25) * mm, "end": v(15, -104.25) * mm});
            skLineSegment(sketch, "E91.MirrorCS", {"start": v(15, -92.25) * mm, "end": v(33.29, -73.96) * mm});
            skLineSegment(sketch, "E92.MirrorCS", {"start": v(-15, -92.25) * mm, "end": v(-33.29, -73.96) * mm});
            skLineSegment(sketch, "E93.MirrorCS", {"start": v(-15, -92.25) * mm, "end": v(-15, -104.25) * mm});
            skLineSegment(sketch, "E94", {"start": v(-33.29, 73.96) * mm, "end": v(0, 73.96) * mm});
            skLineSegment(sketch, "E95", {"start": v(0, 73.96) * mm, "end": v(33.29, 73.96) * mm});
            skLineSegment(sketch, "E96", {"start": v(-33.29, -73.96) * mm, "end": v(0, -73.96) * mm});
            skLineSegment(sketch, "E97", {"start": v(0, -73.96) * mm, "end": v(33.29, -73.96) * mm});
            skSolve(sketch);
        }
        {
            var Q0;
            Q0 = qSketchRegion(id + "F16", true);
            var Q1;
            {var subQ0=sQuery(id+"F0.wireOp",EDGE,"E21.filletArc");var subQ1=sQuery(id+"F0.wireOp",EDGE,"E7");var subQ2=sQuery(id+"F0.wireOp",EDGE,"E6");var subQ3=sQuery(id+"F0.wireOp",EDGE,"E5");var subQ4=sQuery(id+"F0.wireOp",EDGE,"E4");var subQ5=sQuery(id+"F0.wireOp",EDGE,"E22.filletArc");var subQ6=sQuery(id+"F0.wireOp",EDGE,"E1.bottom");var subQ7=sQuery(id+"F0.wireOp",EDGE,"E1.right");var subQ8=sQuery(id+"F0.wireOp",EDGE,"E1.top");var subQ9=sQuery(id+"F0.wireOp",EDGE,"E1.left");var subQ10=sQuery(id+"F0.wireOp",EDGE,"E23.filletArc");var subQ11=sQuery(id+"F0.wireOp",EDGE,"E24.filletArc");Q1=makeQuery(id+"F2.boolean.opBoolean","SPLIT",FACE,{"disambiguationData":[TD([makeQuery(id+"F1.opExtrude","SWEPT_FACE",FACE,{"disambiguationData":[OSD([subQ6])]})])],"derivedFrom":makeQuery(id+"F1.opExtrude","CAP_FACE",FACE,{"disambiguationData":[OSD([subQ6,subQ8,subQ9,subQ7,subQ4,subQ3,subQ2,subQ1,subQ0,subQ5,subQ10,subQ11])],"isStart":true})});}
            extrude(context, id + "F17", {"entities" : qUnion([Q0, Q1]), "depth" : 4.6 * mm});
        }
    });
